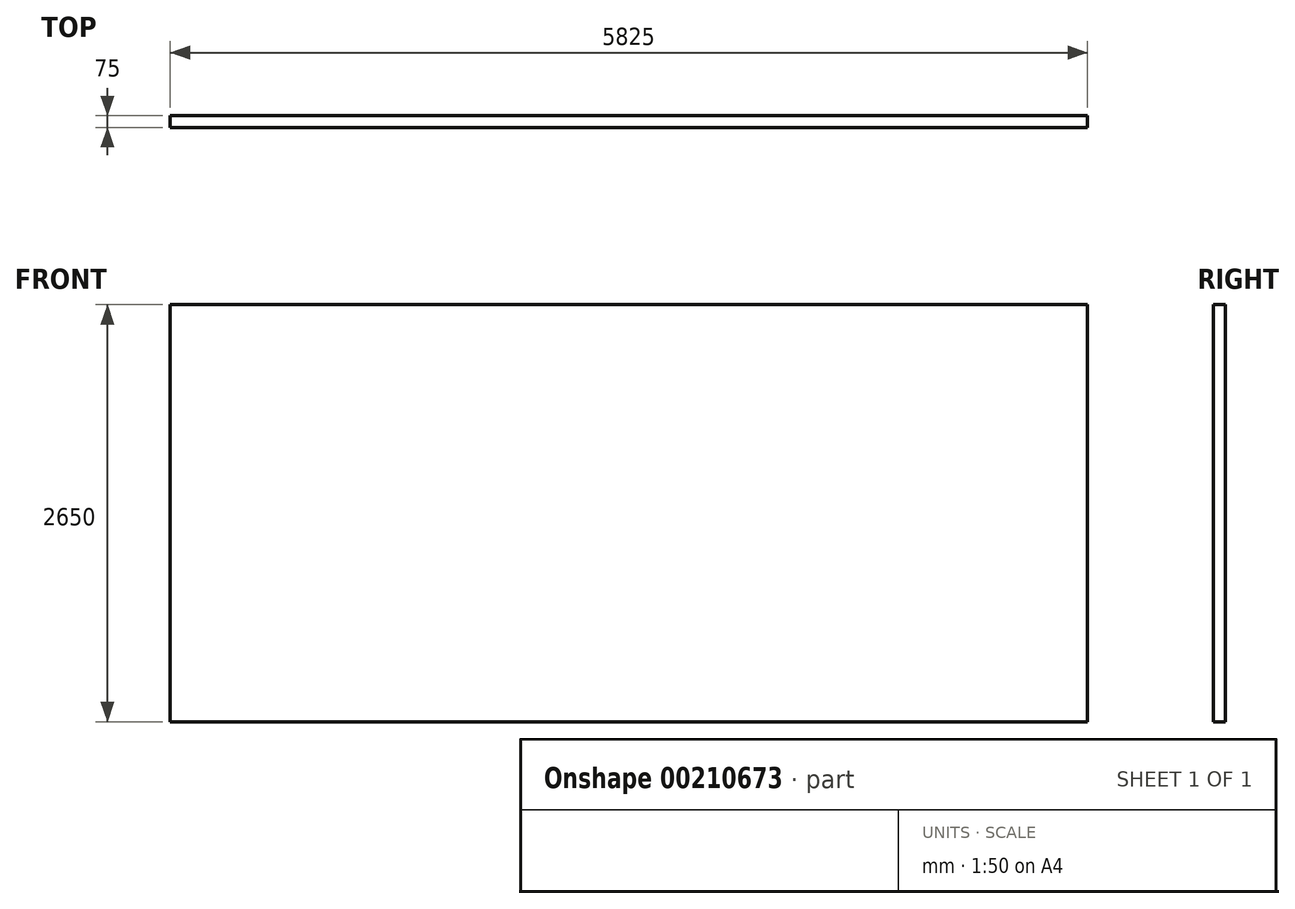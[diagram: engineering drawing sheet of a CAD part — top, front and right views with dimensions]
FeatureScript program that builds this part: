
annotation { "Feature Type Name" : "Feature", "Feature Type Description" : "" }
export const myFeature = defineFeature(function(context is Context, id is Id, definition is map)
    precondition{}
    {
        {
            var Q0;
            Q0=qCreatedBy(makeId("Front.planeOp"),FACE);
            var sketch = newSketch(context, id + "F0", { "sketchPlane" : qUnion([Q0])});
            skLineSegment(sketch, "E0.bottom", {"start": v(0, 0) * mm, "end": v(5825, 0) * mm});
            skLineSegment(sketch, "E0.top", {"start": v(0, 2650) * mm, "end": v(5825, 2650) * mm});
            skLineSegment(sketch, "E0.left", {"start": v(0, 0) * mm, "end": v(0, 2650) * mm});
            skLineSegment(sketch, "E0.right", {"start": v(5825, 0) * mm, "end": v(5825, 2650) * mm});
            skSolve(sketch);
        }
        {
            var Q0;
            Q0=makeQuery(id+"F0.imprint","IMPRINT",FACE,{"disambiguationData":[TD([[makeQuery(id+"F0.imprint","IMPRINT",EDGE,{"derivedFrom":sQuery(id+"F0.wireOp",EDGE,"E0.bottom")}),1.0]])]});
            extrude(context, id + "F1", {"entities" : qUnion([Q0]), "depth" : 75 * mm});
        }
    });
